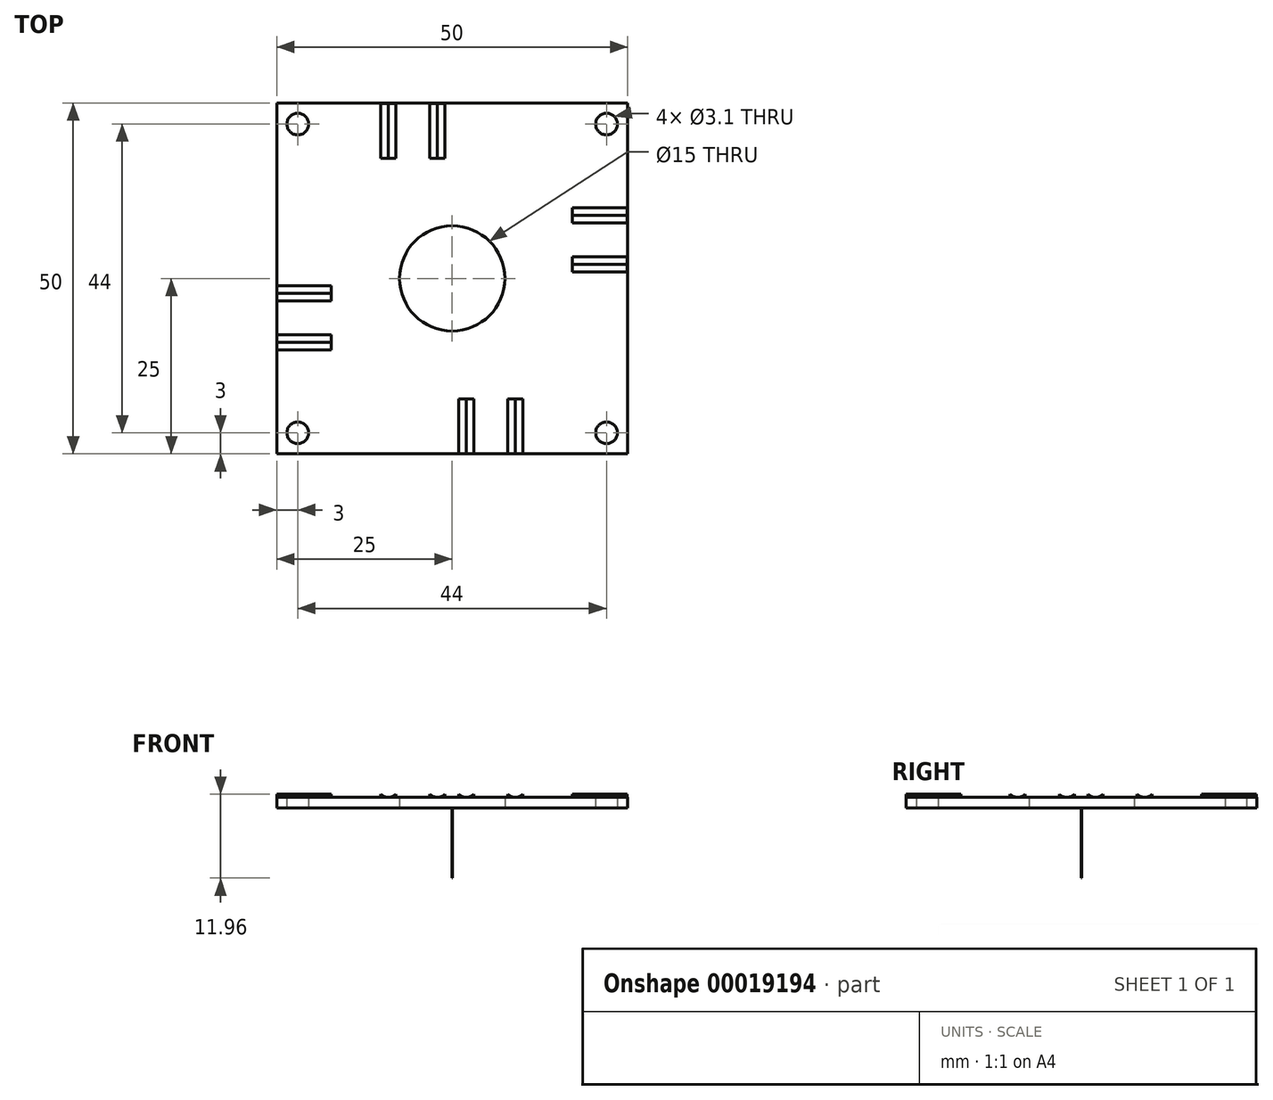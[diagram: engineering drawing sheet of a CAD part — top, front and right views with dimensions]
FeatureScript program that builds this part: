
annotation { "Feature Type Name" : "Feature", "Feature Type Description" : "" }
export const myFeature = defineFeature(function(context is Context, id is Id, definition is map)
    precondition{}
    {
        {
            var Q0;
            Q0=qCreatedBy(makeId("Top.planeOp"),FACE);
            var sketch = newSketch(context, id + "F0", { "sketchPlane" : qUnion([Q0])});
            skLineSegment(sketch, "E0.rect.bottom", {"start": v(-25, 25) * mm, "end": v(25, 25) * mm});
            skLineSegment(sketch, "E0.rect.top", {"start": v(-25, -25) * mm, "end": v(25, -25) * mm});
            skLineSegment(sketch, "E0.rect.left", {"start": v(-25, 25) * mm, "end": v(-25, -25) * mm});
            skLineSegment(sketch, "E0.rect.right", {"start": v(25, 25) * mm, "end": v(25, -25) * mm});
            skPoint(sketch, "E0.rect.middle", {"position": v(0, 0) * mm});
            skCircle(sketch, "E1", {"center": v(0, 0) * mm, "radius": 7.5 * mm});
            skCircle(sketch, "E2", {"center": v(-22, -22) * mm, "radius": 1.55 * mm});
            skCircle(sketch, "E3.MirrorC", {"center": v(22, -22) * mm, "radius": 1.55 * mm});
            skLineSegment(sketch, "E4", {"start": v(0, 0) * mm, "end": v(-25, 0) * mm});
            skLineSegment(sketch, "E5", {"start": v(-25, 0) * mm, "end": v(25, 0) * mm});
            skCircle(sketch, "E6.MirrorC", {"center": v(-22, 22) * mm, "radius": 1.55 * mm});
            skCircle(sketch, "E7.MirrorC", {"center": v(22, 22) * mm, "radius": 1.55 * mm});
            skSolve(sketch);
        }
        {
            var Q0;
            Q0 = qSketchRegion(id + "F0", true);
            extrude(context, id + "F1", {"entities" : qUnion([Q0]), "depth" : 1.5 * mm});
        }
        {
            var Q0;
            Q0=makeQuery(id+"F1.opExtrude","SWEPT_FACE",FACE,{"disambiguationData":[OSD([sQuery(id+"F0.wireOp",EDGE,"E0.rect.top")])]});
            var sketch = newSketch(context, id + "F2", { "sketchPlane" : qUnion([Q0])});
            skLineSegment(sketch, "E8.rect.bottom", {"start": v(3.08, 4.84) * mm, "end": v(0.92, 4.84) * mm, "construction": true});
            skLineSegment(sketch, "E8.rect.top", {"start": v(3.08, 1.5) * mm, "end": v(0.92, 1.5) * mm});
            skLineSegment(sketch, "E8.rect.left", {"start": v(3.08, 4.84) * mm, "end": v(3.08, 1.5) * mm});
            skLineSegment(sketch, "E8.rect.right", {"start": v(0.92, 4.84) * mm, "end": v(0.92, 1.5) * mm});
            skPoint(sketch, "E8.rect.middle", {"position": v(2, 3.17) * mm});
            skLineSegment(sketch, "E9.rect.bottom", {"start": v(10.08, 5.78) * mm, "end": v(7.92, 5.78) * mm, "construction": true});
            skLineSegment(sketch, "E9.rect.top", {"start": v(10.08, 1.5) * mm, "end": v(7.92, 1.5) * mm});
            skLineSegment(sketch, "E9.rect.left", {"start": v(10.08, 5.78) * mm, "end": v(10.08, 1.5) * mm});
            skLineSegment(sketch, "E9.rect.right", {"start": v(7.92, 5.78) * mm, "end": v(7.92, 1.5) * mm});
            skPoint(sketch, "E9.rect.middle", {"position": v(9, 3.64) * mm});
            skArc(sketch, "E10", {"start": v(0.92, 1.96) * mm, "mid": v(2, 1.5) * mm, "end": v(3.08, 1.96) * mm});
            skArc(sketch, "E11", {"start": v(7.92, 1.96) * mm, "mid": v(9, 1.5) * mm, "end": v(10.08, 1.96) * mm});
            skLineSegment(sketch, "E12", {"start": v(-9.06, 1.96) * mm, "end": v(10, 1.96) * mm, "construction": true});
            skLineSegment(sketch, "E13", {"start": v(-25, 0) * mm, "end": v(-25, 28.42) * mm, "construction": true});
            skLineSegment(sketch, "E14", {"start": v(25, 0) * mm, "end": v(25, 26.25) * mm, "construction": true});
            skSolve(sketch);
        }
        {
            var Q0;
            Q0 = qSketchRegion(id + "F2", true);
            extrude(context, id + "F3", {"entities" : qUnion([Q0]), "oppositeDirection" : true, "depth" : 7.8 * mm});
        }
        {
            var Q0;
            Q0=makeQuery(id+"F1.opExtrude","CAP_FACE",FACE,{"disambiguationData":[OSD([sQuery(id+"F0.wireOp",EDGE,"E0.rect.bottom"),sQuery(id+"F0.wireOp",EDGE,"E0.rect.top"),sQuery(id+"F0.wireOp",EDGE,"E0.rect.left"),sQuery(id+"F0.wireOp",EDGE,"E0.rect.right"),sQuery(id+"F0.wireOp",EDGE,"E1"),sQuery(id+"F0.wireOp",EDGE,"E2"),sQuery(id+"F0.wireOp",EDGE,"E3.MirrorC"),sQuery(id+"F0.wireOp",EDGE,"E6.MirrorC"),sQuery(id+"F0.wireOp",EDGE,"E7.MirrorC")])],"isStart":false});
            var sketch = newSketch(context, id + "F4", { "sketchPlane" : qUnion([Q0])});
            skLineSegment(sketch, "E15", {"start": v(0, 25) * mm, "end": v(0, -25) * mm});
            skLineSegment(sketch, "E16", {"start": v(-25, 0) * mm, "end": v(25, 0) * mm});
            skSolve(sketch);
        }
        {
            var Q0;
            Q0=makeQuery(id+"F1.opExtrude","CAP_FACE",FACE,{"disambiguationData":[OSD([sQuery(id+"F0.wireOp",EDGE,"E0.rect.bottom"),sQuery(id+"F0.wireOp",EDGE,"E0.rect.top"),sQuery(id+"F0.wireOp",EDGE,"E0.rect.left"),sQuery(id+"F0.wireOp",EDGE,"E0.rect.right"),sQuery(id+"F0.wireOp",EDGE,"E1"),sQuery(id+"F0.wireOp",EDGE,"E2"),sQuery(id+"F0.wireOp",EDGE,"E3.MirrorC"),sQuery(id+"F0.wireOp",EDGE,"E6.MirrorC"),sQuery(id+"F0.wireOp",EDGE,"E7.MirrorC")])],"isStart":true});
            var sketch = newSketch(context, id + "F5", { "sketchPlane" : qUnion([Q0])});
            skLineSegment(sketch, "E17.rect.bottom", {"start": v(0.05, 0.05) * mm, "end": v(-0.05, 0.05) * mm});
            skLineSegment(sketch, "E17.rect.top", {"start": v(0.05, -0.05) * mm, "end": v(-0.05, -0.05) * mm});
            skLineSegment(sketch, "E17.rect.left", {"start": v(0.05, 0.05) * mm, "end": v(0.05, -0.05) * mm});
            skLineSegment(sketch, "E17.rect.right", {"start": v(-0.05, 0.05) * mm, "end": v(-0.05, -0.05) * mm});
            skPoint(sketch, "E17.rect.middle", {"position": v(0, 0) * mm});
            skSolve(sketch);
        }
        {
            var Q0;
            Q0 = qSketchRegion(id + "F5", true);
            extrude(context, id + "F6", {"entities" : qUnion([Q0]), "depth" : 10 * mm});
        }
        {
            var Q0;
            Q0=makeQuery(id+"Fm028jtNl4Vreql_5.opPattern","COPY",BODY,{"derivedFrom":makeQuery(id+"F3.opExtrude","SWEPT_BODY",BODY,{"disambiguationData":[OSD([sQuery(id+"F2.wireOp",EDGE,"E9.rect.top"),sQuery(id+"F2.wireOp",EDGE,"E9.rect.right"),sQuery(id+"F2.wireOp",EDGE,"E11")])]}),"instanceName":"1"});
            var Q1;
            Q1=makeQuery(id+"Fm028jtNl4Vreql_5.opPattern","COPY",BODY,{"derivedFrom":makeQuery(id+"F3.opExtrude","SWEPT_BODY",BODY,{"disambiguationData":[OSD([sQuery(id+"F2.wireOp",EDGE,"E8.rect.top"),sQuery(id+"F2.wireOp",EDGE,"E8.rect.left"),sQuery(id+"F2.wireOp",EDGE,"E10")])]}),"instanceName":"1"});
            var Q2;
            Q2=makeQuery(id+"F3.opExtrude","SWEPT_BODY",BODY,{"disambiguationData":[OSD([sQuery(id+"F2.wireOp",EDGE,"E8.rect.top"),sQuery(id+"F2.wireOp",EDGE,"E8.rect.right"),sQuery(id+"F2.wireOp",EDGE,"E10")])]});
            var Q3;
            Q3=makeQuery(id+"F3.opExtrude","SWEPT_BODY",BODY,{"disambiguationData":[OSD([sQuery(id+"F2.wireOp",EDGE,"E8.rect.top"),sQuery(id+"F2.wireOp",EDGE,"E8.rect.left"),sQuery(id+"F2.wireOp",EDGE,"E10")])]});
            var Q4;
            Q4=makeQuery(id+"Fm028jtNl4Vreql_5.opPattern","COPY",BODY,{"derivedFrom":makeQuery(id+"F3.opExtrude","SWEPT_BODY",BODY,{"disambiguationData":[OSD([sQuery(id+"F2.wireOp",EDGE,"E9.rect.top"),sQuery(id+"F2.wireOp",EDGE,"E9.rect.left"),sQuery(id+"F2.wireOp",EDGE,"E11")])]}),"instanceName":"1"});
            var Q5;
            Q5=makeQuery(id+"F3.opExtrude","SWEPT_BODY",BODY,{"disambiguationData":[OSD([sQuery(id+"F2.wireOp",EDGE,"E9.rect.top"),sQuery(id+"F2.wireOp",EDGE,"E9.rect.left"),sQuery(id+"F2.wireOp",EDGE,"E11")])]});
            var Q6;
            Q6=makeQuery(id+"F3.opExtrude","SWEPT_BODY",BODY,{"disambiguationData":[OSD([sQuery(id+"F2.wireOp",EDGE,"E9.rect.top"),sQuery(id+"F2.wireOp",EDGE,"E9.rect.right"),sQuery(id+"F2.wireOp",EDGE,"E11")])]});
            var Q7;
            Q7=makeQuery(id+"Fm028jtNl4Vreql_5.opPattern","COPY",BODY,{"derivedFrom":makeQuery(id+"F3.opExtrude","SWEPT_BODY",BODY,{"disambiguationData":[OSD([sQuery(id+"F2.wireOp",EDGE,"E8.rect.top"),sQuery(id+"F2.wireOp",EDGE,"E8.rect.right"),sQuery(id+"F2.wireOp",EDGE,"E10")])]}),"instanceName":"1"});
            var Q8;
            Q8=makeQuery(id+"F6.opExtrude","SWEPT_EDGE",EDGE,{"disambiguationData":[OSD([sQuery(id+"F5.wireOp",EDGE,"E17.rect.bottom"),sQuery(id+"F5.wireOp",EDGE,"E17.rect.right")])]});
            circularPattern(context, id + "F7", {"entities" : qUnion([Q0, Q1, Q2, Q3, Q4, Q5, Q6, Q7]), "axis" : qUnion([Q8]), "angle" : 90 * degree, "instanceCount" : 4});
        }
    });
